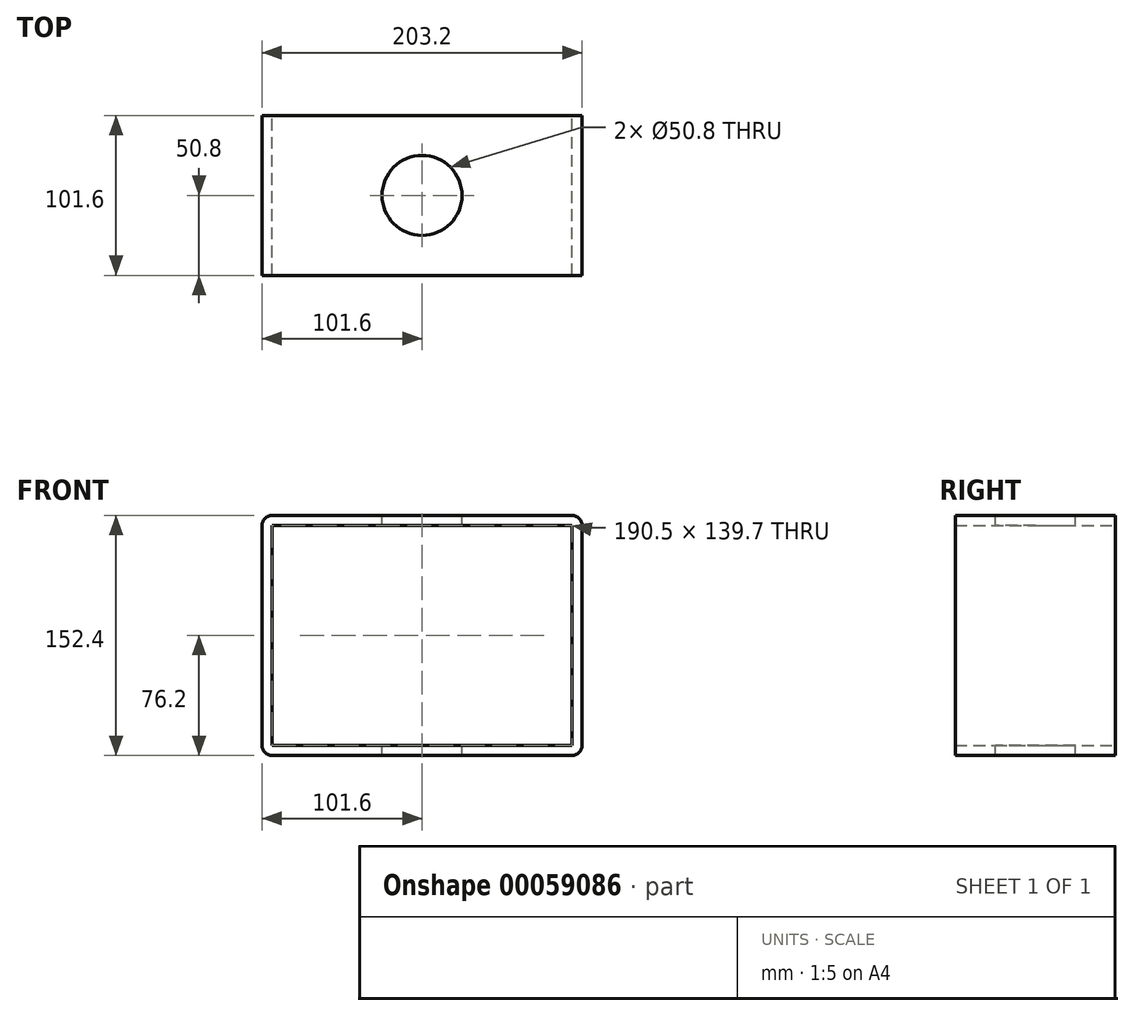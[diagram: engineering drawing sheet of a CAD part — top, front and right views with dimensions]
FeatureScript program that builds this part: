
annotation { "Feature Type Name" : "Feature", "Feature Type Description" : "" }
export const myFeature = defineFeature(function(context is Context, id is Id, definition is map)
    precondition{}
    {
        {
            var Q0;
            Q0=qCreatedBy(makeId("Front.planeOp"),FACE);
            var sketch = newSketch(context, id + "F0", { "sketchPlane" : qUnion([Q0])});
            skLineSegment(sketch, "E0.rect.bottom", {"start": v(95.25, -76.2) * mm, "end": v(-95.25, -76.2) * mm});
            skLineSegment(sketch, "E0.rect.top", {"start": v(95.25, 76.2) * mm, "end": v(-95.25, 76.2) * mm});
            skLineSegment(sketch, "E0.rect.left", {"start": v(101.6, -69.85) * mm, "end": v(101.6, 69.85) * mm});
            skLineSegment(sketch, "E0.rect.right", {"start": v(-101.6, -69.85) * mm, "end": v(-101.6, 69.85) * mm});
            skPoint(sketch, "E0.rect.middle", {"position": v(0, 0) * mm});
            skPoint(sketch, "E1.visualSharp", {"position": v(-101.6, 76.2) * mm});
            skArc(sketch, "E1.filletArc", {"start": v(-95.25, 76.2) * mm, "mid": v(-99.74, 74.34) * mm, "end": v(-101.6, 69.85) * mm});
            skPoint(sketch, "E2.visualSharp", {"position": v(101.6, 76.2) * mm});
            skArc(sketch, "E2.filletArc", {"start": v(101.6, 69.85) * mm, "mid": v(99.74, 74.34) * mm, "end": v(95.25, 76.2) * mm});
            skPoint(sketch, "E3.visualSharp", {"position": v(101.6, -76.2) * mm});
            skArc(sketch, "E3.filletArc", {"start": v(95.25, -76.2) * mm, "mid": v(99.74, -74.34) * mm, "end": v(101.6, -69.85) * mm});
            skPoint(sketch, "E4.visualSharp", {"position": v(-101.6, -76.2) * mm});
            skArc(sketch, "E4.filletArc", {"start": v(-101.6, -69.85) * mm, "mid": v(-99.74, -74.34) * mm, "end": v(-95.25, -76.2) * mm});
            skLineSegment(sketch, "E5.0", {"start": v(95.25, 69.85) * mm, "end": v(-95.25, 69.85) * mm});
            skLineSegment(sketch, "E6.0", {"start": v(95.25, -69.85) * mm, "end": v(95.25, 69.85) * mm});
            skLineSegment(sketch, "E7.0", {"start": v(95.25, -69.85) * mm, "end": v(-95.25, -69.85) * mm});
            skLineSegment(sketch, "E8.0", {"start": v(-95.25, -69.85) * mm, "end": v(-95.25, 69.85) * mm});
            skSolve(sketch);
        }
        {
            var Q0;
            Q0 = qSketchRegion(id + "F0", true);
            extrude(context, id + "F1", {"entities" : qUnion([Q0]), "depth" : 101.6 * mm});
        }
        {
            var Q0;
            Q0=makeQuery(id+"F1.opExtrude","SWEPT_FACE",FACE,{"disambiguationData":[OSD([sQuery(id+"F0.wireOp",EDGE,"E0.rect.top")])]});
            var sketch = newSketch(context, id + "F2", { "sketchPlane" : qUnion([Q0])});
            skLineSegment(sketch, "E9.0", {"start": v(44.45, -50.8) * mm, "end": v(-44.45, -50.8) * mm, "construction": true});
            skLineSegment(sketch, "E9.1", {"start": v(44.45, -50.8) * mm, "end": v(44.45, -50.8) * mm});
            skLineSegment(sketch, "E9.2", {"start": v(-44.45, -50.8) * mm, "end": v(44.45, -50.8) * mm, "construction": true});
            skLineSegment(sketch, "E9.3", {"start": v(-44.45, -50.8) * mm, "end": v(-44.45, -50.8) * mm});
            skCircle(sketch, "E10", {"center": v(0, -50.8) * mm, "radius": 25.4 * mm});
            skSolve(sketch);
        }
        {
            var Q0;
            Q0 = qSketchRegion(id + "F2", true);
            extrude(context, id + "F3", {"entities" : qUnion([Q0]), "operationType" : NewBodyOperationType.REMOVE, "endBound" : BoundingType.THROUGH_ALL, "oppositeDirection" : true, "depth" : 25.4 * mm});
        }
    });
